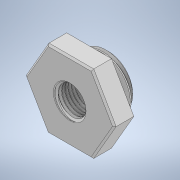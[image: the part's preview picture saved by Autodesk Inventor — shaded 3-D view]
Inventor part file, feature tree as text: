
AUTODESK INVENTOR PART (.ipt)
format: ipt  version: 2021 (Build 250183000, 183)  size: 516,608 bytes
history: native  units: mm
features: sketch x10, extrude x7, helix x2, chamfer x2, revolve x1, projected_geometry x1
ambient origin geometry x8: Origin, YZ Plane, XZ Plane, XY Plane, X Axis, Y Axis, Z Axis, Center Point
bodies: Solid1 (feature_tree)
feature tree (23):
  extrude  "Extrusion1"  Depth=8.0mm TaperAngle=0.0deg
  extrude  "Extrusion2"  Depth=8.0mm TaperAngle=0.0deg
  helix  "Coil1"  [1 undecoded]
  extrude  "Extrusion3"  Depth=23.5mm
  revolve  "Revolution1"  Angle=60.0deg
  extrude  "Extrusion6"  Depth=8.0mm TaperAngle=0.0deg
  chamfer  "Chamfer1"  Distance=18.0mm
  helix  "Coil2"  [1 undecoded]
  extrude  "Extrusion7"  Depth=10.0mm
  chamfer  "Chamfer2"  [1 undecoded]
  extrude  "Extrusion4"  Depth=10.0mm
  extrude  "Extrusion5"  TaperAngle=0.0deg  [1 undecoded]
  sketch  "Sketch1"  dims[d0=32.0mm d1=8.0mm d2=0.0mm]
  sketch  "Sketch2"  dims[d3=19.85mm d4=8.0mm d5=0.0mm d6=19.85mm]
  sketch  "Sketch3"  dims[d7=21.8mm d8=23.5mm]
  sketch  "Sketch4"  dims[d9=30.0deg d10=60.0deg]
  sketch  "Sketch5"  dims[d11=1.5mm]
  sketch  "Sketch6"  dims[d12=3.0mm d13=15.0mm d14=10.0mm d15=0.0mm d16=90.0deg d17=90.0deg d18=0.0mm d19=0.0mm d20=8.0mm d21=0.0mm]
  sketch  "Sketch7"  dims[d22=10.0mm]
  projected_geometry  "Projected Loop1"
  sketch  "Sketch8"  dims[d23=11.8mm]
  sketch  "Sketch10"  dims[d24=45.0deg]
  sketch  "Sketch11"  dims[d25=90.0deg d26=18.0mm d27=35.0mm d28=0.0mm d29=1.5mm d30=0.0mm d31=0.0mm d32=11.495mm d33=0.0mm d34=0.0mm d35=1.0mm d36=2.0mm d37=45.0deg d38=5.7475mm d39=6.175mm d40=6.6mm d41=9.599311mm d42=4.799655mm d43=0.668421mm d44=1.336842mm d45=20.0mm d46=10.0mm d47=0.0mm d48=90.0deg d49=90.0deg d50=0.0mm d51=0.0mm d52=13.5mm d53=3.0mm d54=0.0mm d55=0.7mm d56=2.0mm d57=45.0deg]
note: 4 required parameter values undecoded (feature->parameter linkage not recoverable at this tier; creation-order binding heuristic only, values carry confidence <= 0.55)
